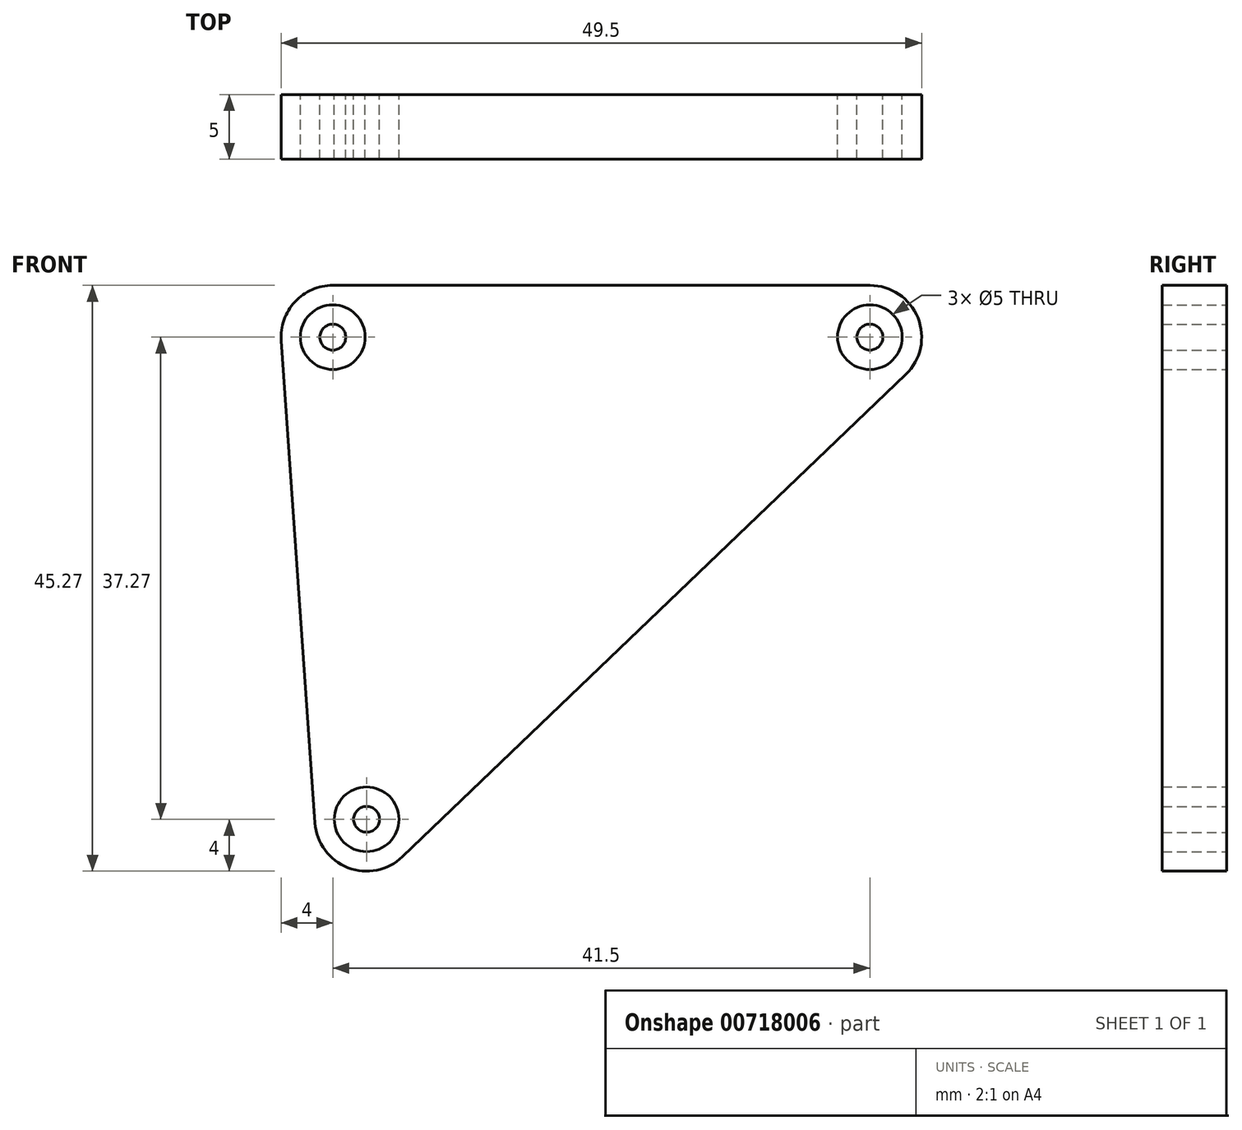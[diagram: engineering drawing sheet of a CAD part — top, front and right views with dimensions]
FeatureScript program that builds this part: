
annotation { "Feature Type Name" : "Feature", "Feature Type Description" : "" }
export const myFeature = defineFeature(function(context is Context, id is Id, definition is map)
    precondition{}
    {
        {
            var Q0;
            Q0=qCreatedBy(makeId("Front.planeOp"),FACE);
            var sketch = newSketch(context, id + "F0", { "sketchPlane" : qUnion([Q0])});
            skArc(sketch, "E0", {"start": v(-15.71, 6.74) * mm, "mid": v(-18.64, 5.47) * mm, "end": v(-19.7, 2.46) * mm});
            skArc(sketch, "E1", {"start": v(28.56, -0.15) * mm, "mid": v(29.5, 4.23) * mm, "end": v(25.79, 6.74) * mm});
            skArc(sketch, "E2", {"start": v(-17.1, -34.8) * mm, "mid": v(-14.54, -38.26) * mm, "end": v(-10.33, -37.42) * mm});
            skLineSegment(sketch, "E3", {"start": v(-15.71, 6.74) * mm, "end": v(25.79, 6.74) * mm});
            skLineSegment(sketch, "E4", {"start": v(-19.7, 2.46) * mm, "end": v(-17.1, -34.8) * mm});
            skLineSegment(sketch, "E5", {"start": v(28.56, -0.15) * mm, "end": v(-10.33, -37.42) * mm});
            skCircle(sketch, "E6", {"center": v(-15.71, 2.74) * mm, "radius": 2.5 * mm});
            skCircle(sketch, "E7", {"center": v(-15.71, 2.74) * mm, "radius": 1 * mm});
            skCircle(sketch, "E8", {"center": v(25.79, 2.74) * mm, "radius": 2.5 * mm});
            skCircle(sketch, "E9", {"center": v(25.79, 2.74) * mm, "radius": 1 * mm});
            skCircle(sketch, "E10", {"center": v(-13.1, -34.53) * mm, "radius": 1 * mm});
            skCircle(sketch, "E11", {"center": v(-13.1, -34.53) * mm, "radius": 2.5 * mm});
            skSolve(sketch);
        }
        {
            var Q0;
            Q0 = qSketchRegion(id + "F0", true);
            var Q1;
            Q1=makeQuery(id+"F0.imprint","IMPRINT",FACE,{"disambiguationData":[TD([[makeQuery(id+"F0.imprint","IMPRINT",EDGE,{"derivedFrom":sQuery(id+"F0.wireOp",EDGE,"E7")}),1.0]])]});
            var Q2;
            Q2=makeQuery(id+"F0.imprint","IMPRINT",FACE,{"disambiguationData":[TD([[makeQuery(id+"F0.imprint","IMPRINT",EDGE,{"derivedFrom":sQuery(id+"F0.wireOp",EDGE,"E9")}),1.0]])]});
            var Q3;
            Q3=makeQuery(id+"F0.imprint","IMPRINT",FACE,{"disambiguationData":[TD([[makeQuery(id+"F0.imprint","IMPRINT",EDGE,{"derivedFrom":sQuery(id+"F0.wireOp",EDGE,"E10")}),1.0]])]});
            extrude(context, id + "F1", {"entities" : qUnion([Q0, Q1, Q2, Q3]), "depth" : 5 * mm, "offsetDistance" : 25 * mm});
        }
    });
